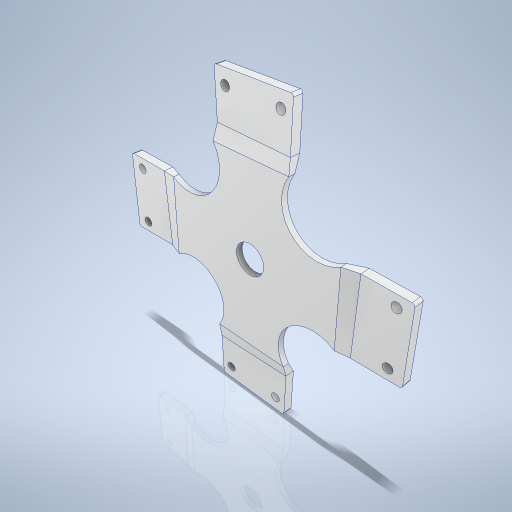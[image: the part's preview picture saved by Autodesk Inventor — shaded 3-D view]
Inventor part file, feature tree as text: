
AUTODESK INVENTOR PART (.ipt)
format: ipt  version: 2024.2 (Build 282272000, 272)  size: 497,664 bytes
history: native  units: mm
features: sketch x7, other x4, fillet x4, pattern_circular x3, hole x2, plane x2, loft x2, extrude x1, projected_geometry x1
ambient origin geometry x8: Origin, YZ Plane, XZ Plane, XY Plane, X Axis, Y Axis, Z Axis, Center Point
bodies: Volumenkörper1 (feature_tree)
feature tree (26):
  other  "Fläche1"
  extrude  "Extrusion3"  Depth=2.0mm
  pattern_circular  "Runde Anordnung2"  Count=4 Angle=360.0deg
  hole  "Bohrung1"  [1 undecoded]
  plane  "Arbeitsebene1"
  plane  "Arbeitsebene2"
  sketch  "Skizze6"  dims[d19=10.0mm d20=0.0mm d21=40.0mm d22=360.0deg]
  sketch  "Skizze7"  dims[d24=10.0mm d25=6.0mm d26=4.0mm d27=2.0mm d28=90.0deg d29=2.0mm d30=20.594885mm]
  loft  "Erhebung1"
  loft  "Erhebung2"
  pattern_circular  "Runde Anordnung3"  Angle=90.0deg  [1 undecoded]
  fillet  "Rundung1"  [1 undecoded]
  fillet  "Rundung2"  Radius=25.0mm
  fillet  "Rundung3"  Radius=3.0mm
  fillet  "Rundung4"  [1 undecoded]
  hole  "Bohrung6"  [1 undecoded]
  pattern_circular  "Runde Anordnung4"  Count=4 Angle=360.0deg
  sketch  "Skizze1"  dims[d0=64.0mm d1=2.0mm]
  other  "Grobblech1"
  sketch  "Skizze4"  dims[d15=45.0deg]
  sketch  "Skizze5"  dims[d18=12.0mm]
  projected_geometry  "Projizierte Kontur1"
  sketch  "Skizze8"  dims[d31=49.0mm d32=34.0mm d34=19.198622mm]
  other  "Kanten2"
  other  "Kanten3"
  sketch  "Skizze14"  dims[d35=25.0mm d36=3.0mm d37=0.0mm d38=90.0deg d39=0.0mm d40=90.0deg d41=90.0deg d42=25.0mm d43=3.0mm d44=0.0mm d45=90.0deg d46=0.0mm d47=90.0deg d48=40.0mm d49=360.0deg d51=0.8mm d52=0.8mm d53=0.8mm d54=0.8mm d107=3.5mm d108=4.5mm d109=4.5mm d110=3.5mm d111=3.0mm d112=6.0mm d113=4.0mm d114=2.0mm d115=90.0deg d116=2.0mm d117=20.594885mm d118=40.0mm d119=360.0deg]
note: 5 required parameter values undecoded (feature->parameter linkage not recoverable at this tier; creation-order binding heuristic only, values carry confidence <= 0.55)
